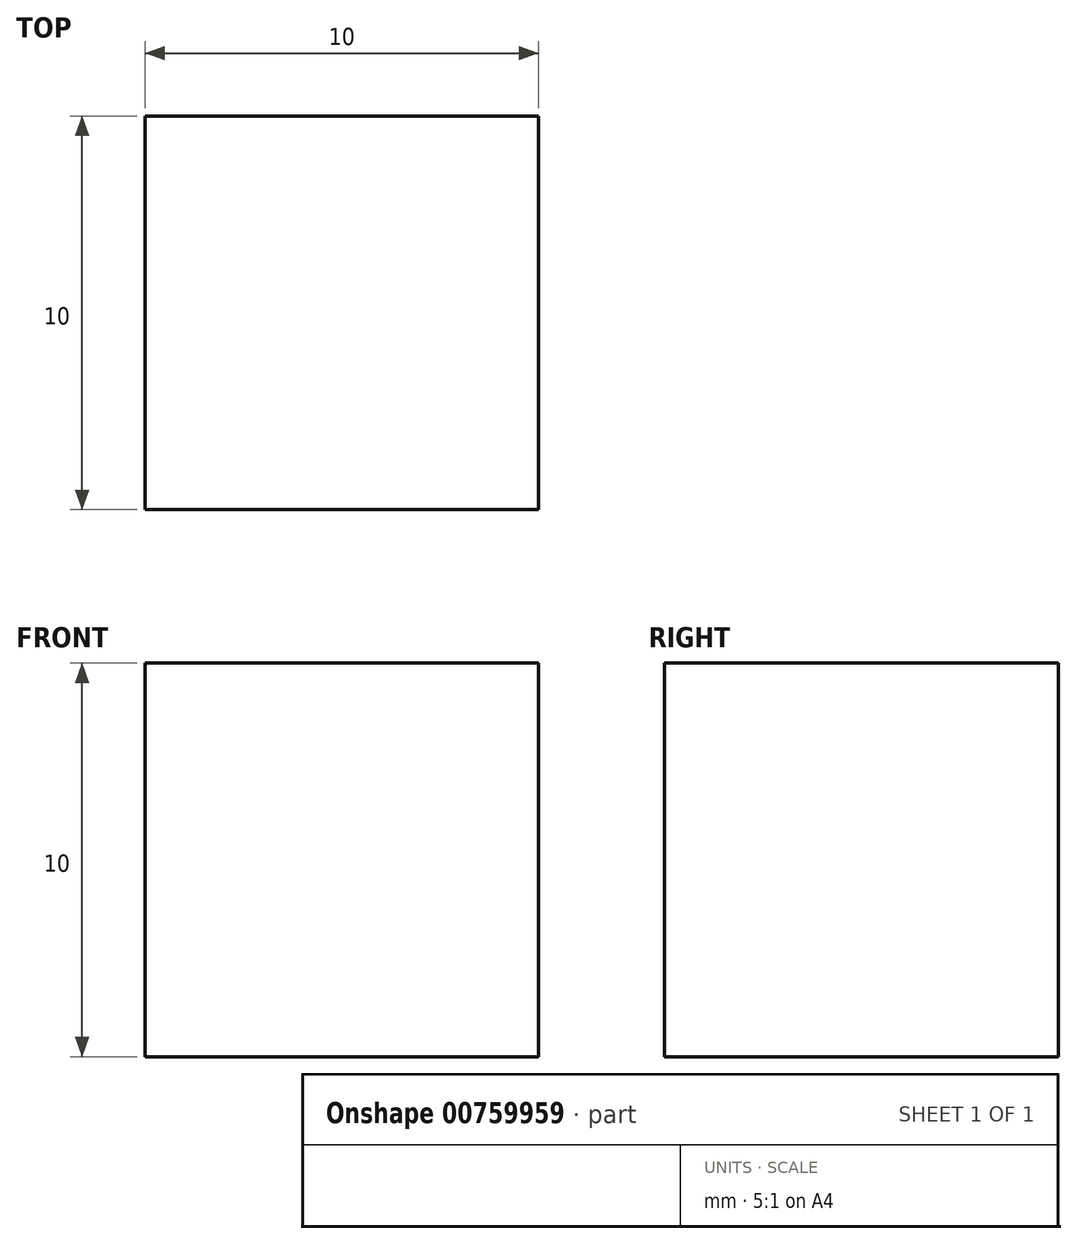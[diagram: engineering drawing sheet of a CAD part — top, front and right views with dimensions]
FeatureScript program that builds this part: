
annotation { "Feature Type Name" : "Feature", "Feature Type Description" : "" }
export const myFeature = defineFeature(function(context is Context, id is Id, definition is map)
    precondition{}
    {
        {
            var Q0;
            Q0=qCreatedBy(makeId("Front.planeOp"),FACE);
            var sketch = newSketch(context, id + "F0", { "sketchPlane" : qUnion([Q0])});
            skLineSegment(sketch, "E0.bottom", {"start": v(-5, 5) * mm, "end": v(5, 5) * mm});
            skLineSegment(sketch, "E0.top", {"start": v(-5, -5) * mm, "end": v(5, -5) * mm});
            skLineSegment(sketch, "E0.left", {"start": v(-5, 5) * mm, "end": v(-5, -5) * mm});
            skLineSegment(sketch, "E0.right", {"start": v(5, 5) * mm, "end": v(5, -5) * mm});
            skPoint(sketch, "E0.middle", {"position": v(0, 0) * mm});
            skSolve(sketch);
        }
        {
            var Q0;
            Q0 = qSketchRegion(id + "F0", true);
            extrude(context, id + "F1", {"entities" : qUnion([Q0]), "depth" : 10 * mm, "offsetDistance" : 25 * mm});
        }
    });
